# Revit family: INFRA_AQUA_ECO_TYPE_3
name_source: partatom
category: Mechanical Equipment
revit_build: Autodesk Revit 2015 (Build: 20140606_1530(x64)
units: mm (PartAtom-declared; Revit-internal decimal feet)

## types (2) — shared parameters
Ceiling_height = 350 mm  [stored 1.14829 ft]
Description = Radiant heater, waterfed, type INFRA AQUA ECO
Heating_load = 0 W
Hook_panel = 28 mm
Ifc_Description = Radiant heater, waterfed, type INFRA AQUA ECO
Ifc_Export_as = IfcSpaceHeater
Ifc_Export_type = RADIATOR
Manufacturer = MARK Climate Technology
Model = Type 1
Panel_height = 42 mm  [stored 0.137795 ft]
Pipe_spacing = 75 mm
Product_serie = INFRA AQUA ECO
Space_between_panels = 25 mm  [stored 0.082021 ft]
URL = http://www.markclimate.co.uk
Width_per_panel = 306 mm  [stored 1.00394 ft]

## per-type parameters (varying)
| type | Length | Material | Material_index |
| Type 3 L=4000 | 4000 mm  [stored 13.1234 ft] | <By Category> | 4 |
| Type 3 L=6000 | 6000 mm  [stored 19.685 ft] | Aluminium | 6 |

note: [stored X ft] marks values corroborated as IEEE doubles in the binary element streams (Revit-internal decimal feet)

## geometry (parser evidence)
native form markers: Sweep x18
no freeform markers — native parametric forms only
